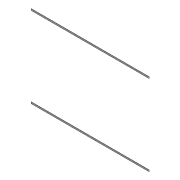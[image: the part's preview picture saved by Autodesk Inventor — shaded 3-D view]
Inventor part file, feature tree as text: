
AUTODESK INVENTOR PART (.ipt)
format: ipt  version: 2012 (Build 160160000, 160)  size: 72,192 bytes
history: native  units: in
note: dims shown in document units (in); Inventor stores cm internally (conversion verified against a paired STEP export)
features: extrude x1, pattern_linear x1, sketch x1
ambient origin geometry x8: Origin, YZ Plane, XZ Plane, XY Plane, X Axis, Y Axis, Z Axis, Center Point
bodies: Solid1 (feature_tree)
feature tree (3):
  extrude  "Extrusion1"  Depth=145.0in
  pattern_linear  "Rectangular Pattern1"  Spacing1=0.188in  [1 undecoded]
  sketch  "Sketch1"  dims[d0=2.0in d1=145.0in d2=0.188in d3=0.0in d4=0.7874in d6=99.0in]
note: 1 required parameter value undecoded (feature->parameter linkage not recoverable at this tier; creation-order binding heuristic only, values carry confidence <= 0.55)
